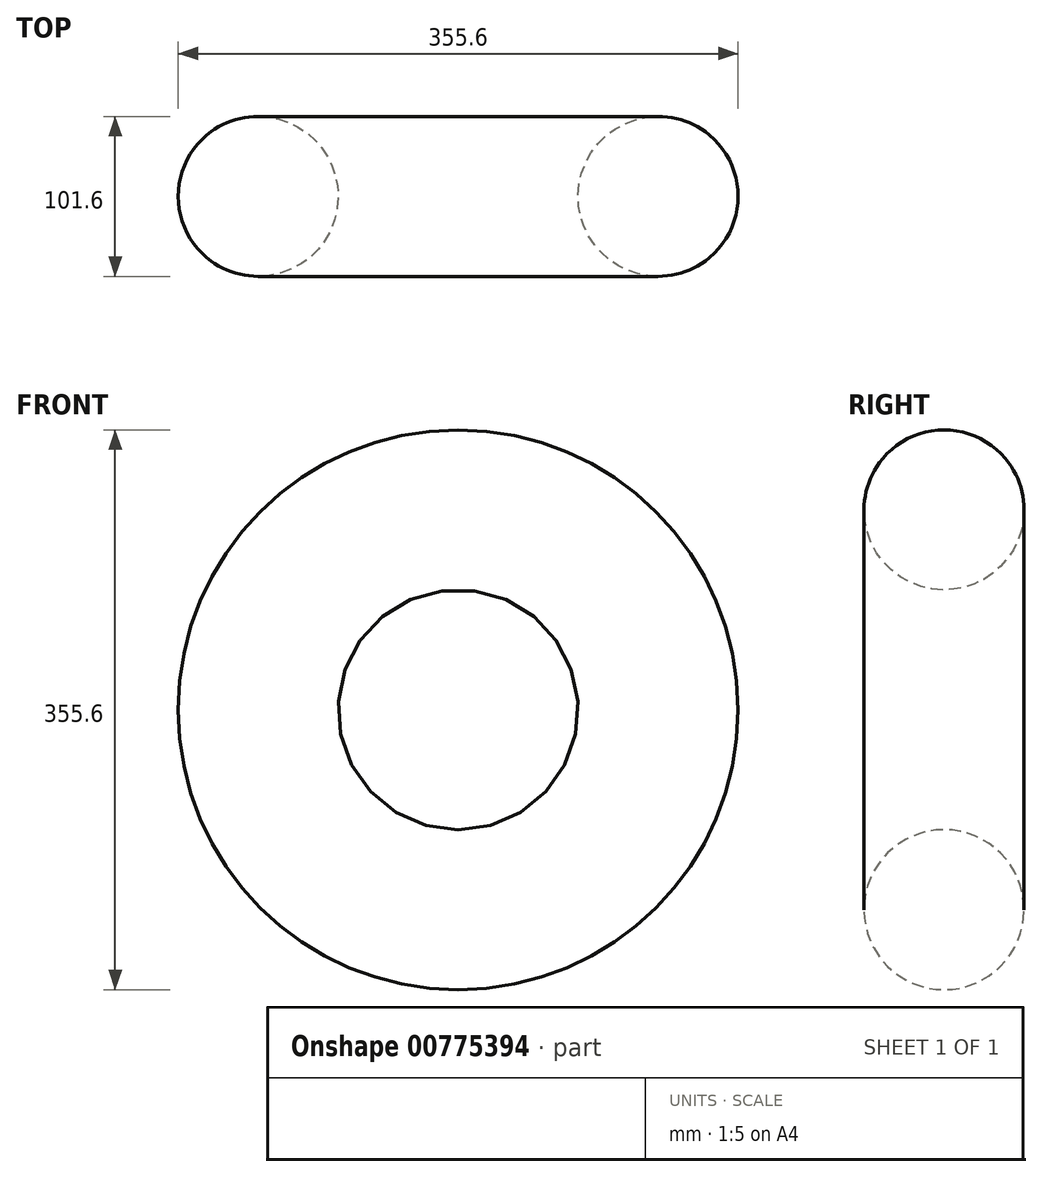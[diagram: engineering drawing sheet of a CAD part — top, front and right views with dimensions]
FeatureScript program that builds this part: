
annotation { "Feature Type Name" : "Feature", "Feature Type Description" : "" }
export const myFeature = defineFeature(function(context is Context, id is Id, definition is map)
    precondition{}
    {
        {
            var Q0;
            Q0=qCreatedBy(makeId("Top.planeOp"),FACE);
            var sketch = newSketch(context, id + "F0", { "sketchPlane" : qUnion([Q0])});
            skCircle(sketch, "E0", {"center": v(0, 0) * mm, "radius": 50.8 * mm});
            skLineSegment(sketch, "E1", {"start": v(-127, -100.65) * mm, "end": v(-127, 107.08) * mm, "construction": true});
            skSolve(sketch);
        }
        {
            var Q0;
            Q0=makeQuery(id+"F0.imprint","IMPRINT",FACE,{"disambiguationData":[TD([[makeQuery(id+"F0.imprint","IMPRINT",EDGE,{"derivedFrom":sQuery(id+"F0.wireOp",EDGE,"E0")}),1.0]])]});
            var Q1;
            Q1=sQuery(id+"F0.wireOp",EDGE,"E1");
            revolve(context, id + "F1", {"surfaceOperationType" : NewSurfaceOperationType.NEW, "entities" : qUnion([Q0]), "axis" : qUnion([Q1]), "revolveType" : RevolveType.FULL});
        }
    });
